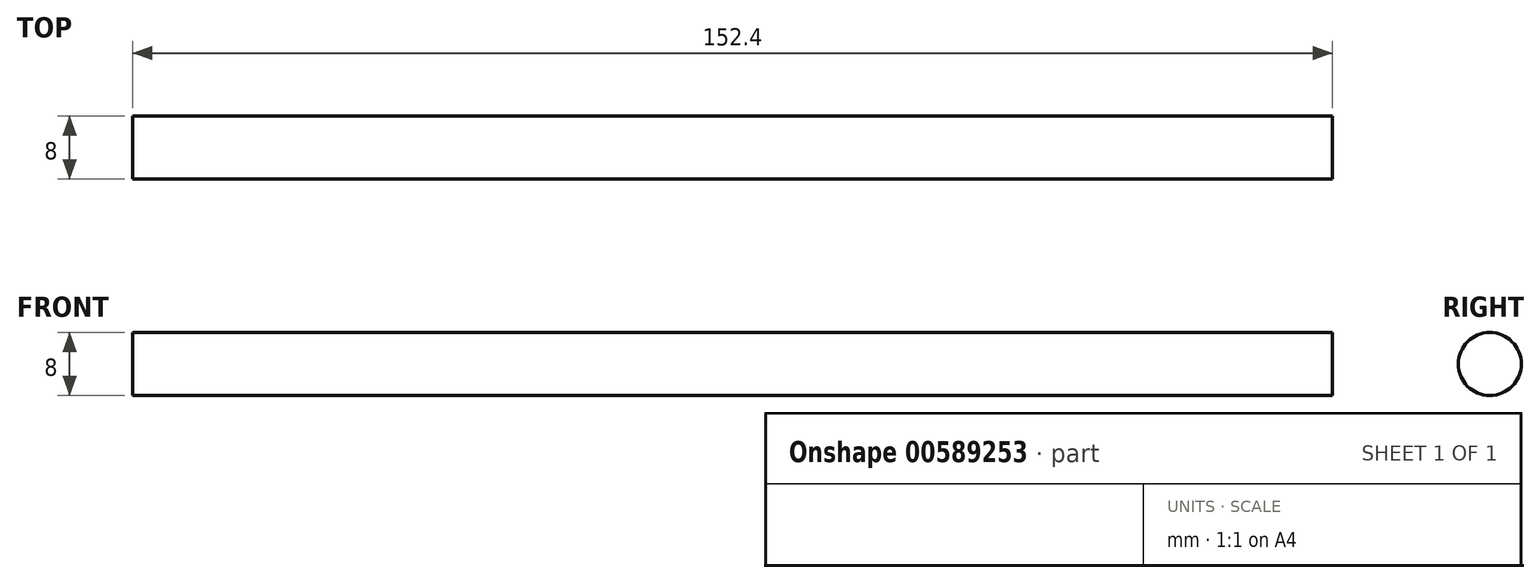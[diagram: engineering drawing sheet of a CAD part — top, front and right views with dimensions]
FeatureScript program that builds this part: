
annotation { "Feature Type Name" : "Feature", "Feature Type Description" : "" }
export const myFeature = defineFeature(function(context is Context, id is Id, definition is map)
    precondition{}
    {
        {
            var Q0;
            Q0=qCreatedBy(makeId("Right.planeOp"),FACE);
            var sketch = newSketch(context, id + "F0", { "sketchPlane" : qUnion([Q0])});
            skCircle(sketch, "E0", {"center": v(0, 0) * mm, "radius": 4 * mm});
            skSolve(sketch);
        }
        {
            var Q0;
            Q0=makeQuery(id+"F0.imprint","IMPRINT",FACE,{"disambiguationData":[TD([[makeQuery(id+"F0.imprint","IMPRINT",EDGE,{"derivedFrom":sQuery(id+"F0.wireOp",EDGE,"E0")}),1.0]])]});
            extrude(context, id + "F1", {"entities" : qUnion([Q0]), "depth" : (6 * 25.4) * mm, "offsetDistance" : 25 * mm});
        }
    });
